# Revit family: Zumtobel SLOTLIGHT Round
name_source: partatom
category: Lighting Fixtures
revit_build: Autodesk Revit 2016 (Build: 20150220_1215(x64)
units: mm (PartAtom-declared; Revit-internal decimal feet)

## family parameters
Cut with Voids When Loaded = No
Host = Face
Light Source = Yes
OmniClass Number = 23.80.70.11
OmniClass Title = Luminaries for Internal Lighting
Part Type = Normal
Room Calculation Point = No
Round Connector Dimension = Use Diameter
Shared = No

## types (3) — shared parameters
Assembly Code = D5020200
Color Filter = 16777215
Description = LED lumaire
Dimming Lamp Color Temperature Shift = <None>
Emit Shape Visible in Rendering = No
Height = 85 mm
Lamp = LED
Manufacturer = Zumtobel Lighting
Tilt Angle = -90.00°
URL = http://www.zumtobel.com
Voltage = 0 V
zero-valued in all types: Default Elevation

## per-type parameters (varying)
| type | Apparent Load | Emit from Circle Diameter | Length | Model | Photometric Web File | Suspension Diameter | Width |
| SLOIN R D D800 | 49 VA | 800 mm | 800 mm | 42187659 | 42187659_(STD_LEO).IES | 774 mm | 800 mm |
| SLOIN R D 1200 | 69 VA | 1200 mm | 1200 mm | 42187676 | 42187676_(STD_LEO).IES | 1174 mm  [stored 3.85171 ft] | 1200 mm |
| SLOIN R D 1500 | 92 VA | 1500 mm | 1500 mm | 42187692 | 42187692_(STD_LEO).IES | 1474 mm | 1500 mm |

note: [stored X ft] marks values corroborated as IEEE doubles in the binary element streams (Revit-internal decimal feet)

## geometry (parser evidence)
native form markers: Sweep x4
no freeform markers — native parametric forms only
